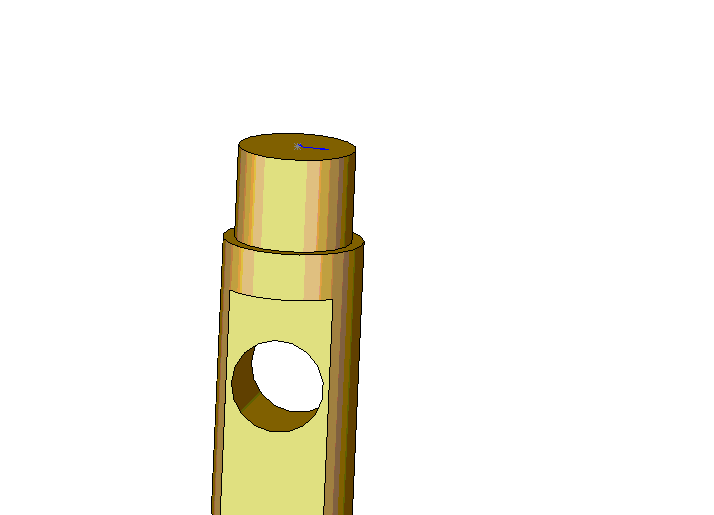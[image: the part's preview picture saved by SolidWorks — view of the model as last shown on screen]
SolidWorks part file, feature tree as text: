
SOLIDWORKS PART (.sldprt)
format: sldprt  version: not decoded by parser v0  size: 177,664 bytes
history: native  units: mm
features: sketch x4, cut_extrude x3, extrude x1 (+10 scaffold rows collapsed)
feature tree (18):
  scaffold x10  (default folders/planes/origin — collapsed)
  sketch  "Sketch1"  dims[D1=19.05mm]
  extrude  "Extrude1"  Depth=50.8mm
  sketch  "Sketch2"  dims[D1=12.7mm]
  cut_extrude  "Cut-Extrude1"  Depth=31.75mm
  sketch  "Sketch3"  dims[D1=12.7mm D2=19.05mm]
  cut_extrude  "Cut-Extrude2"  [1 undecoded]
  sketch  "Sketch4"  dims[D1=15.875mm]
  cut_extrude  "Cut-Extrude3"  Depth=12.7mm
decode coverage: 7 of 8 modeling features carry decoded parameters
note: 1 parameter value undecoded
note: suppression state not decoded; provenance and decode notes live in map.json
